# Revit family: Lives Shelf_Coat hanger Unit 900W450D2236H_ML1EHLN_m01
name_source: partatom
category: Furniture
units: mm (PartAtom-declared; Revit-internal decimal feet)

## family parameters
Always vertical = Yes
Cut with Voids When Loaded = No
OmniClass Number = 23.40.20.00
OmniClass Title = General Furniture and Specialties
Room Calculation Point = No
Shared = No
Work Plane-Based = No

## types (14) — shared parameters
Assembly Code = E2020200
D = 17.7 "
H = 88 "
Keynote = 12490
Manufacturer = 株式会社オカムラ
URL = http://www.okamura.co.jp
W = 35.4 "
区分 = シェルフ
製品カテゴリ = クリエイティブファニチュア
製品コード/色仕様 = ML1EHE

## per-type parameters (varying)
| type | 天板 | 支柱 |
| MDY7（プライズウッドライト/ブラック） | okm_MX61 | okm_Z25 |
| MDY8（プライズウッドミディアム/ブラック） | okm_MX62 | okm_Z25 |
| MDY9（プライズウッドダーク/ブラック） | okm_MX63 | okm_Z25 |
| MU03（プライズウッドライト/ネオホワイト） | okm_MX61 | okm_ZA75 |
| MU04（プライズウッドミディアム/ネオホワイト） | okm_MX62 | okm_ZA75 |
| MU05（プライズウッドダーク/ネオホワイト） | okm_MX63 | okm_ZA75 |
| MGM4（ビンテージエルム/ネオホワイト） | okm_MEP4 | okm_ZA75 |
| MGM1（チョークドエルム/ネオホワイト） | okm_MEP1 | okm_ZA75 |
| MGM2（ソーンオーク/ネオホワイト） | okm_MEP2 | okm_ZA75 |
| MGM3（ラスティックパイン/ネオホワイト） | okm_MEP3 | okm_ZA75 |
| MGL4（ビンテージエルム/ブラック） | okm_MEP4 | okm_Z25 |
| MGL1（チョークドエルム/ブラック） | okm_MEP1 | okm_Z25 |
| MGL2（ソーンオーク/ブラック） | okm_MEP2 | okm_Z25 |
| MGL3（ラスティックパイン/ブラック） | okm_MEP3 | okm_Z25 |
